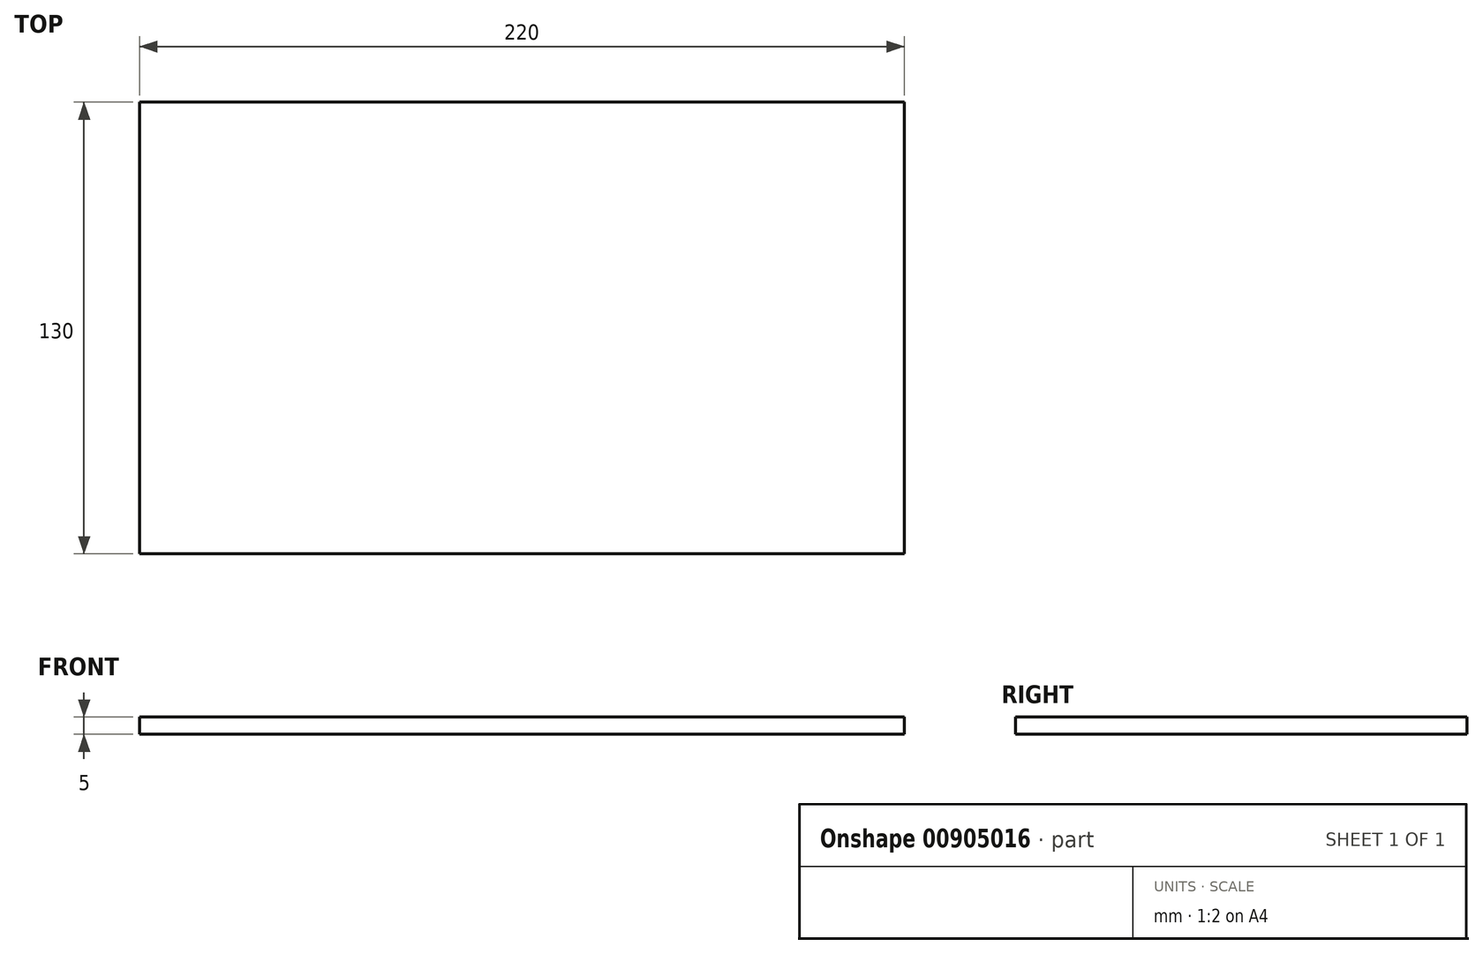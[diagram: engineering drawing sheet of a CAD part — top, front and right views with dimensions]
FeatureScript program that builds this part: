
annotation { "Feature Type Name" : "Feature", "Feature Type Description" : "" }
export const myFeature = defineFeature(function(context is Context, id is Id, definition is map)
    precondition{}
    {
        {
            var Q0;
            Q0=qCreatedBy(makeId("Top.planeOp"),FACE);
            var sketch = newSketch(context, id + "F0", { "sketchPlane" : qUnion([Q0])});
            skLineSegment(sketch, "E0.bottom", {"start": v(110, 65) * mm, "end": v(-110, 65) * mm});
            skLineSegment(sketch, "E0.top", {"start": v(110, -65) * mm, "end": v(-110, -65) * mm});
            skLineSegment(sketch, "E0.left", {"start": v(110, 65) * mm, "end": v(110, -65) * mm});
            skLineSegment(sketch, "E0.right", {"start": v(-110, 65) * mm, "end": v(-110, -65) * mm});
            skPoint(sketch, "E0.middle", {"position": v(0, 0) * mm});
            skSolve(sketch);
        }
        {
            var Q0;
            Q0 = qSketchRegion(id + "F0", true);
            extrude(context, id + "F1", {"entities" : qUnion([Q0]), "oppositeDirection" : true, "depth" : 5 * mm, "offsetDistance" : 25 * mm});
        }
    });
